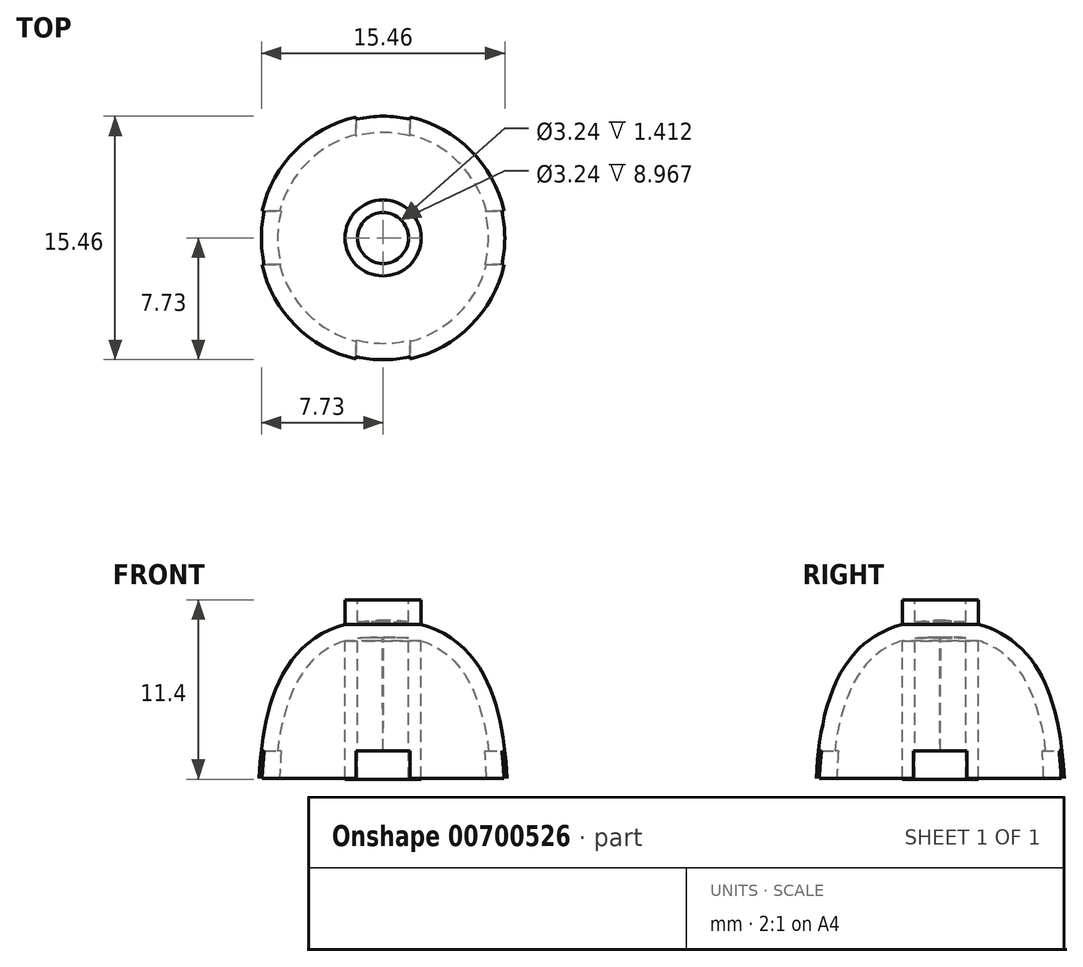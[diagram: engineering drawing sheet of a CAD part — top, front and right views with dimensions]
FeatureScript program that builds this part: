
annotation { "Feature Type Name" : "Feature", "Feature Type Description" : "" }
export const myFeature = defineFeature(function(context is Context, id is Id, definition is map)
    precondition{}
    {
        {
            var Q0;
            Q0=qCreatedBy(makeId("Right.planeOp"),FACE);
            var sketch = newSketch(context, id + "F0", { "sketchPlane" : qUnion([Q0])});
            skLineSegment(sketch, "E0", {"start": v(0, 10.02) * mm, "end": v(0, 0.02) * mm});
            skLineSegment(sketch, "E1", {"start": v(0, 0.02) * mm, "end": v(7.87, 0.02) * mm});
            skFitSpline(sketch, "E2", {"points": [v(0, 10.02) * mm, v(7.87, 0.02) * mm], "startDerivative": vector(20.44, 0.7) * mm, "endDerivative": vector(0.6, -11.4) * mm});
            skLineSegment(sketch, "E3", {"start": v(0, 12.54) * mm, "end": v(0, -2.5) * mm, "construction": true});
            skFitSpline(sketch, "E4.0", {"points": [v(0.04, 8.94) * mm, v(0.8, 8.97) * mm, v(2.12, 8.83) * mm, v(3.58, 8.22) * mm, v(4.67, 7.29) * mm, v(5.5, 6.06) * mm, v(6.1, 4.6) * mm, v(6.6, 2.49) * mm, v(6.74, 0.89) * mm, v(6.8, -0.04) * mm]});
            skLineSegment(sketch, "E5", {"start": v(0.04, 8.94) * mm, "end": v(0, 0.02) * mm});
            skSolve(sketch);
        }
        {
            var Q0;
            Q0=makeQuery(id+"F0.imprint","IMPRINT",FACE,{"disambiguationData":[TD([[makeQuery(id+"F0.imprint","IMPRINT",EDGE,{"derivedFrom":sQuery(id+"F0.wireOp",EDGE,"E0")}),1.0]])]});
            var Q1;
            Q1=sQuery(id+"F0.wireOp",EDGE,"E0");
            revolve(context, id + "F1", {"entities" : qUnion([Q0]), "axis" : qUnion([Q1]), "revolveType" : RevolveType.FULL});
        }
        {
            var Q0;
            Q0=qCreatedBy(makeId("Top.planeOp"),FACE);
            cPlane(context, id + "F2", {"entities" : qUnion([Q0]), "cplaneType" : CPlaneType.OFFSET, "offset" : 11.35 * mm, "width" : 150 * mm, "height" : 150 * mm});
        }
        {
            var Q0;
            Q0=qCreatedBy(id+"F2.planeOp",FACE);
            var sketch = newSketch(context, id + "F3", { "sketchPlane" : qUnion([Q0])});
            skCircle(sketch, "E6", {"center": v(0, 0) * mm, "radius": 2.42 * mm});
            skCircle(sketch, "E7", {"center": v(0, 0) * mm, "radius": 1.62 * mm});
            skSolve(sketch);
        }
        {
            var Q0;
            Q0=qCreatedBy(makeId("Front.planeOp"),FACE);
            cPlane(context, id + "F4", {"entities" : qUnion([Q0]), "cplaneType" : CPlaneType.OFFSET, "offset" : 7.9 * mm, "oppositeDirection" : true, "width" : 150 * mm, "height" : 150 * mm});
        }
        {
            var Q0;
            Q0=qCreatedBy(id+"F4.planeOp",FACE);
            var sketch = newSketch(context, id + "F5", { "sketchPlane" : qUnion([Q0])});
            skLineSegment(sketch, "E8.bottom", {"start": v(-1.7, 0) * mm, "end": v(1.7, 0) * mm});
            skLineSegment(sketch, "E8.top", {"start": v(-1.7, 1.75) * mm, "end": v(1.7, 1.75) * mm});
            skLineSegment(sketch, "E8.left", {"start": v(-1.7, 0) * mm, "end": v(-1.7, 1.75) * mm});
            skLineSegment(sketch, "E8.right", {"start": v(1.7, 0) * mm, "end": v(1.7, 1.75) * mm});
            skSolve(sketch);
        }
        {
            var Q0;
            Q0=makeQuery(id+"F5.imprint","IMPRINT",FACE,{"disambiguationData":[TD([[makeQuery(id+"F5.imprint","IMPRINT",EDGE,{"derivedFrom":sQuery(id+"F5.wireOp",EDGE,"E8.bottom")}),1.0]])]});
            extrude(context, id + "F6", {"entities" : qUnion([Q0]), "operationType" : NewBodyOperationType.REMOVE, "endBound" : BoundingType.THROUGH_ALL, "depth" : 25 * mm, "offsetDistance" : 25 * mm});
        }
        {
            var Q0;
            Q0=qCreatedBy(makeId("Right.planeOp"),FACE);
            cPlane(context, id + "F7", {"entities" : qUnion([Q0]), "cplaneType" : CPlaneType.OFFSET, "offset" : 7.9 * mm, "width" : 150 * mm, "height" : 150 * mm});
        }
        {
            var Q0;
            Q0=qCreatedBy(id+"F7.planeOp",FACE);
            var sketch = newSketch(context, id + "F8", { "sketchPlane" : qUnion([Q0])});
            skLineSegment(sketch, "E9.bottom", {"start": v(-1.7, 0) * mm, "end": v(1.7, 0) * mm});
            skLineSegment(sketch, "E9.top", {"start": v(-1.7, 1.75) * mm, "end": v(1.7, 1.75) * mm});
            skLineSegment(sketch, "E9.left", {"start": v(-1.7, 0) * mm, "end": v(-1.7, 1.75) * mm});
            skLineSegment(sketch, "E9.right", {"start": v(1.7, 0) * mm, "end": v(1.7, 1.75) * mm});
            skSolve(sketch);
        }
        {
            var Q0;
            Q0=makeQuery(id+"F8.imprint","IMPRINT",FACE,{"disambiguationData":[TD([[makeQuery(id+"F8.imprint","IMPRINT",EDGE,{"derivedFrom":sQuery(id+"F8.wireOp",EDGE,"E9.bottom")}),1.0]])]});
            extrude(context, id + "F9", {"entities" : qUnion([Q0]), "operationType" : NewBodyOperationType.REMOVE, "endBound" : BoundingType.THROUGH_ALL, "oppositeDirection" : true, "depth" : 25 * mm, "offsetDistance" : 25 * mm});
        }
        {
            var Q0;
            Q0 = qSketchRegion(id + "F3", true);
            var Q1;
            Q1=makeQuery(id+"F1.opRevolve","SWEPT_FACE",FACE,{"disambiguationData":[OSD([sQuery(id+"F0.wireOp",EDGE,"E2")])]});
            extrude(context, id + "F10", {"entities" : qUnion([Q0]), "operationType" : NewBodyOperationType.ADD, "oppositeDirection" : true, "depth" : 11.4 * mm, "endBoundEntityFace" : qUnion([Q1]), "offsetDistance" : 25 * mm});
        }
    });
